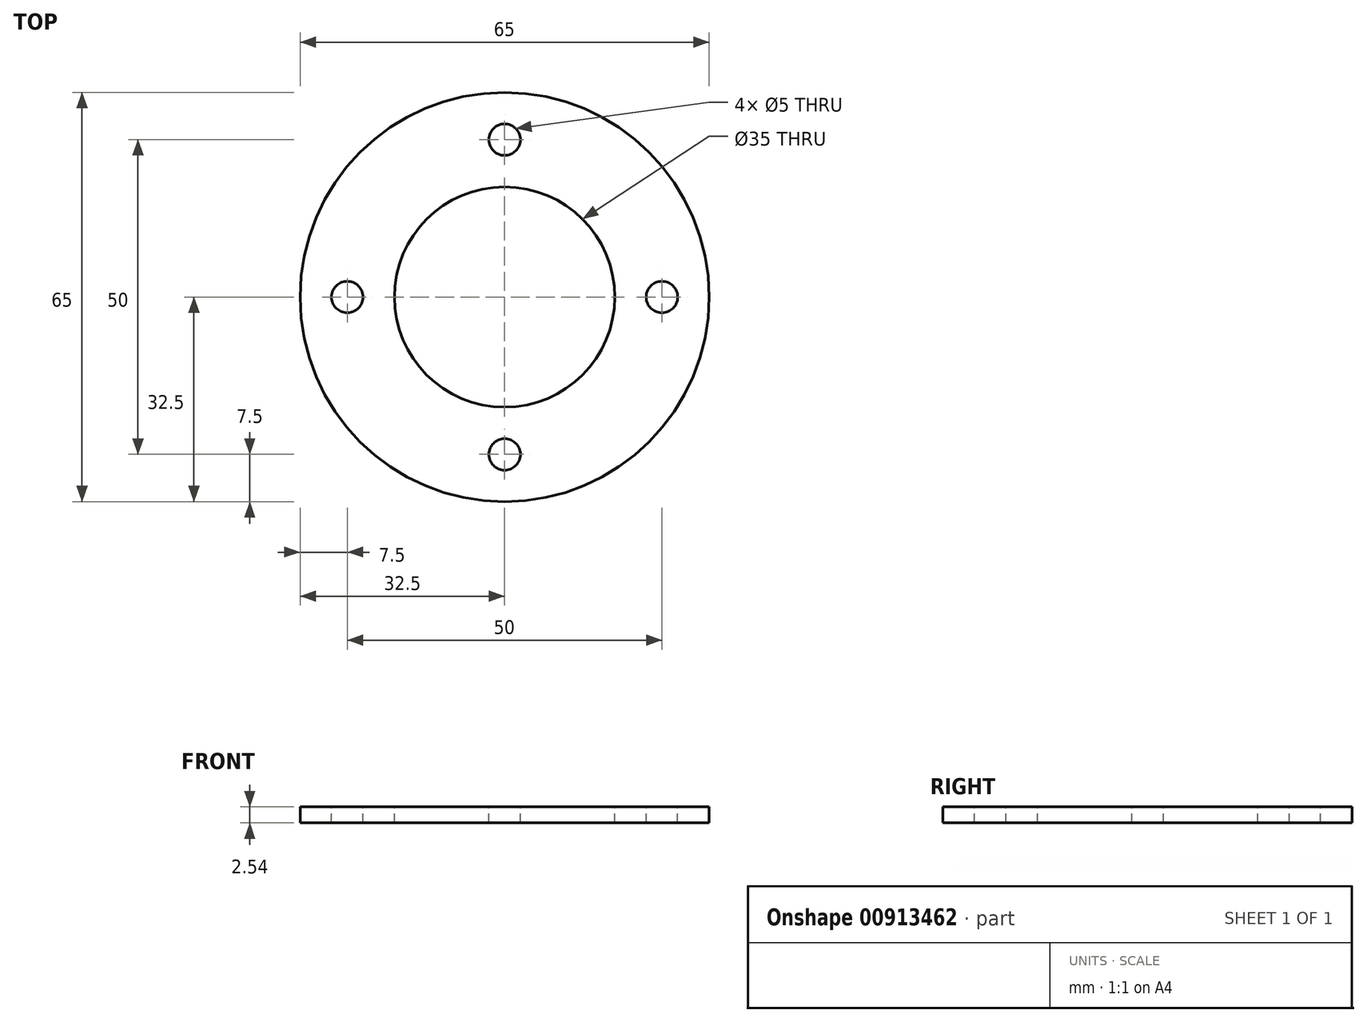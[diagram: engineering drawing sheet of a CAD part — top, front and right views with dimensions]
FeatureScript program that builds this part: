
annotation { "Feature Type Name" : "Feature", "Feature Type Description" : "" }
export const myFeature = defineFeature(function(context is Context, id is Id, definition is map)
    precondition{}
    {
        {
            var Q0;
            Q0=qCreatedBy(makeId("Top.planeOp"),FACE);
            var sketch = newSketch(context, id + "F0", { "sketchPlane" : qUnion([Q0])});
            skCircle(sketch, "E0", {"center": v(0, 0) * mm, "radius": 32.5 * mm});
            skSolve(sketch);
        }
        {
            var Q0;
            Q0 = qSketchRegion(id + "F0", true);
            extrude(context, id + "F1", {"entities" : qUnion([Q0]), "depth" : 2.54 * mm, "offsetDistance" : 25.4 * mm});
        }
        {
            var Q0;
            Q0=makeQuery(id+"F1.opExtrude","CAP_FACE",FACE,{"disambiguationData":[OSD([sQuery(id+"F0.wireOp",EDGE,"E0")])],"isStart":false});
            var sketch = newSketch(context, id + "F2", { "sketchPlane" : qUnion([Q0])});
            skPoint(sketch, "E1", {"position": v(0, 25) * mm});
            skPoint(sketch, "E2", {"position": v(25, 0) * mm});
            skPoint(sketch, "E3", {"position": v(0, -25) * mm});
            skPoint(sketch, "E4", {"position": v(-25, 0) * mm});
            skSolve(sketch);
        }
        {
            var Q0;
            Q0=sQuery(id+"F2.wireOp",VERTEX,"E2");
            var Q1;
            Q1=sQuery(id+"F2.wireOp",VERTEX,"E4");
            var Q2;
            Q2=sQuery(id+"F2.wireOp",VERTEX,"E3");
            var Q3;
            Q3=sQuery(id+"F2.wireOp",VERTEX,"E1");
            var Q4;
            Q4=makeQuery(id+"F1.opExtrude","SWEPT_BODY",BODY,{"disambiguationData":[OSD([sQuery(id+"F0.wireOp",EDGE,"E0")])]});
            hole(context, id + "F3", {"style" : HoleStyle.SIMPLE, "endStyle" : HoleEndStyle.THROUGH, "standardTappedOrClearance" : lookupTablePath({ "standard" : "ISO", "engagement" : "75%", "pitch" : "1 mm", "size" : "M6", "type" : "Tapped" }), "standardBlindInLast" : lookupTablePath({ "standard" : "ISO", "engagement" : "75%", "pitch" : "1 mm", "size" : "M6", "type" : "Tapped" }), "holeDiameter" : 5 * mm, "majorDiameter" : 6 * mm, "showTappedDepth" : true, "isTappedThrough" : true, "tappedDepth" : 12.7 * mm, "tapClearance" : 3, "startFromSketch" : true, "locations" : qUnion([Q0, Q1, Q2, Q3]), "scope" : qUnion([Q4])});
        }
        {
            var Q0;
            Q0=makeQuery(id+"F1.opExtrude","CAP_FACE",FACE,{"disambiguationData":[OSD([sQuery(id+"F0.wireOp",EDGE,"E0")])],"isStart":false});
            var sketch = newSketch(context, id + "F4", { "sketchPlane" : qUnion([Q0])});
            skCircle(sketch, "E5", {"center": v(0, 0) * mm, "radius": 17.5 * mm});
            skSolve(sketch);
        }
        {
            var Q0;
            Q0 = qSketchRegion(id + "F4", true);
            extrude(context, id + "F5", {"entities" : qUnion([Q0]), "operationType" : NewBodyOperationType.REMOVE, "endBound" : BoundingType.THROUGH_ALL, "oppositeDirection" : true, "depth" : 25.4 * mm, "offsetDistance" : 25.4 * mm});
        }
    });
